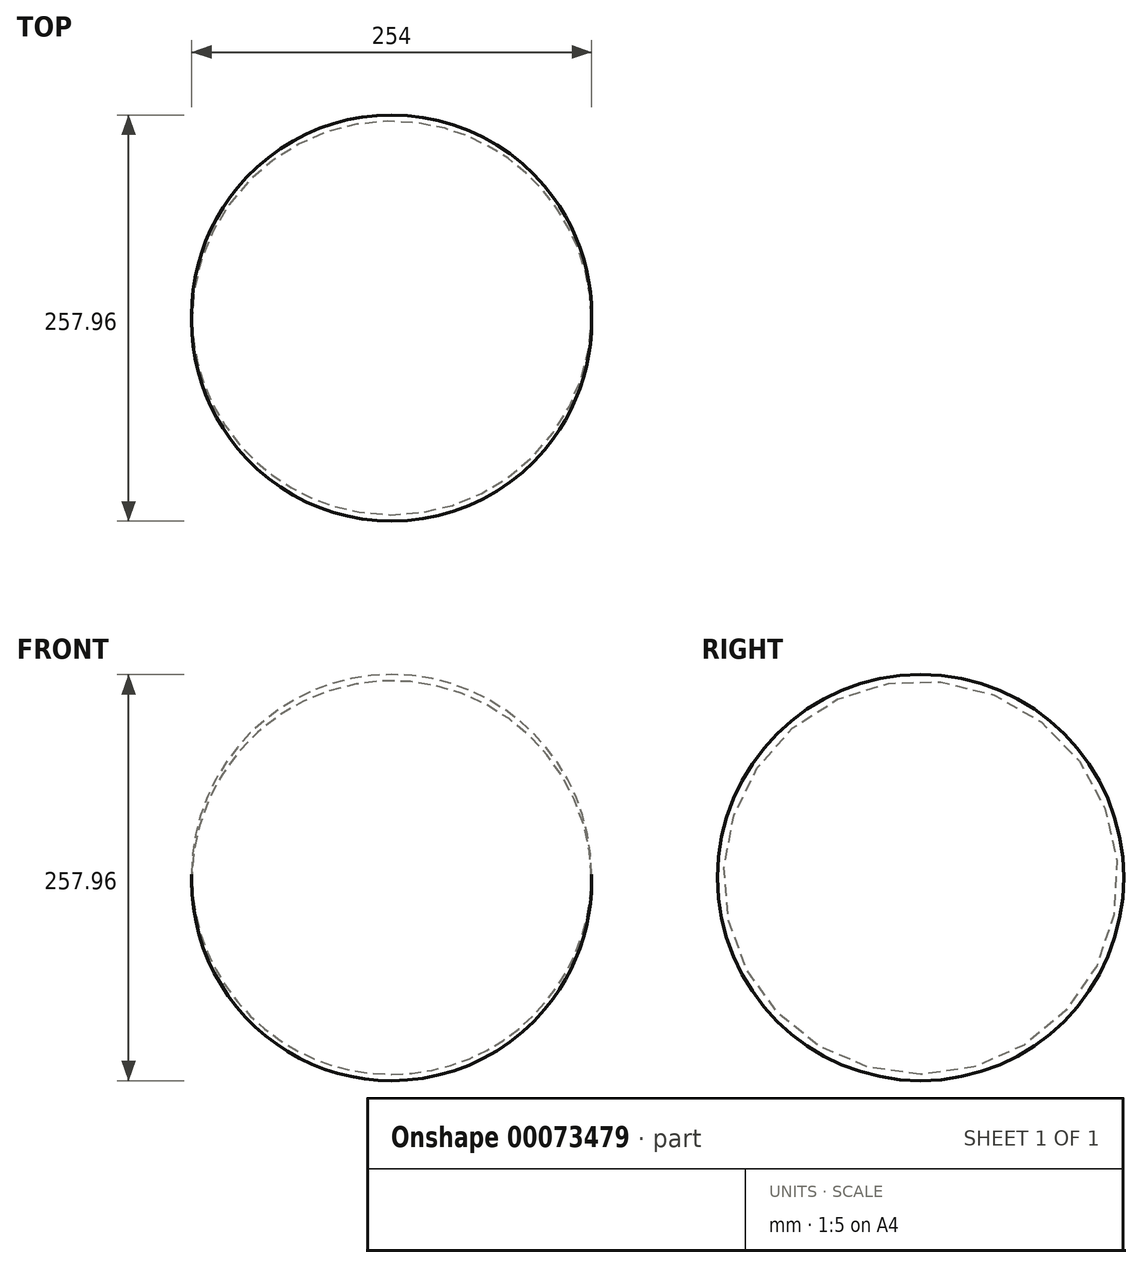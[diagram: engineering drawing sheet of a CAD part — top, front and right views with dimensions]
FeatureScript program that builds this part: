
annotation { "Feature Type Name" : "Feature", "Feature Type Description" : "" }
export const myFeature = defineFeature(function(context is Context, id is Id, definition is map)
    precondition{}
    {
        {
            var Q0;
            Q0=qCreatedBy(makeId("Front.planeOp"),FACE);
            var sketch = newSketch(context, id + "F0", { "sketchPlane" : qUnion([Q0])});
            skArc(sketch, "E0", {"start": v(120.85, 0) * mm, "mid": v(-6.13, 128.98) * mm, "end": v(-133.11, 0) * mm});
            skLineSegment(sketch, "E1", {"start": v(-133.11, 0) * mm, "end": v(120.85, 0) * mm});
            skSolve(sketch);
        }
        {
            var Q0;
            Q0=makeQuery(id+"F0.imprint","IMPRINT",FACE,{"disambiguationData":[TD([[makeQuery(id+"F0.imprint","IMPRINT",EDGE,{"derivedFrom":sQuery(id+"F0.wireOp",EDGE,"E0")}),1.0]])]});
            var Q1;
            Q1=sQuery(id+"F0.wireOp",EDGE,"E1");
            revolve(context, id + "F1", {"entities" : qUnion([Q0]), "axis" : qUnion([Q1]), "revolveType" : RevolveType.FULL});
        }
    });
